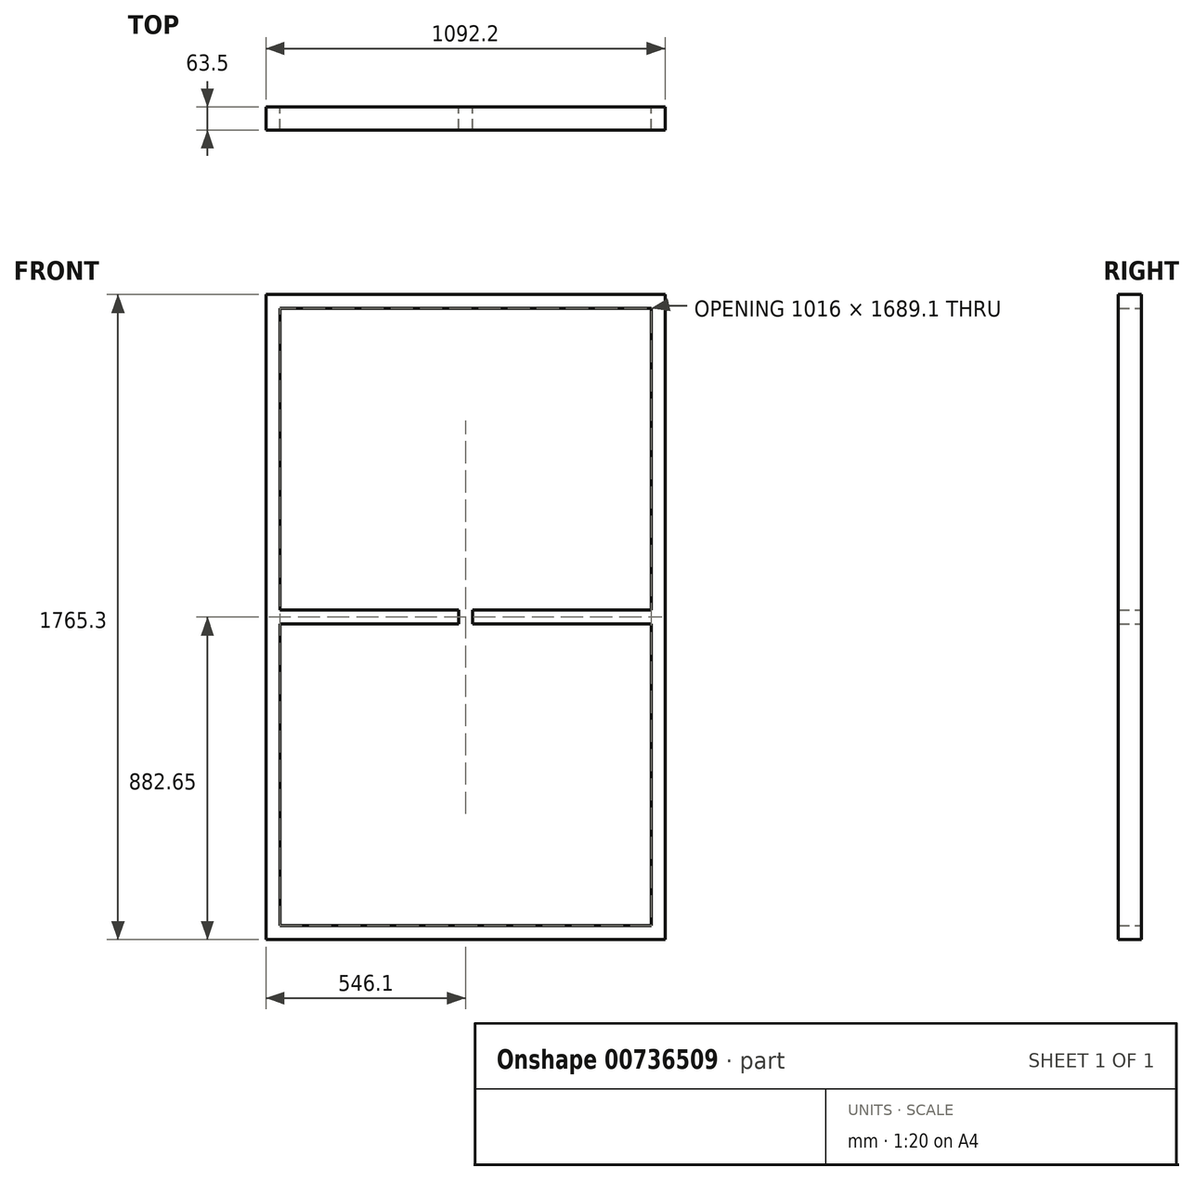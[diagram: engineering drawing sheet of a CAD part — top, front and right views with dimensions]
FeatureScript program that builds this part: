
annotation { "Feature Type Name" : "Feature", "Feature Type Description" : "" }
export const myFeature = defineFeature(function(context is Context, id is Id, definition is map)
    precondition{}
    {
        {
            var Q0;
            Q0=qCreatedBy(makeId("Front.planeOp"),FACE);
            var sketch = newSketch(context, id + "F0", { "sketchPlane" : qUnion([Q0])});
            skLineSegment(sketch, "E0.bottom", {"start": v(546.1, 882.65) * mm, "end": v(-546.1, 882.65) * mm});
            skLineSegment(sketch, "E0.top", {"start": v(546.1, -882.65) * mm, "end": v(-546.1, -882.65) * mm});
            skLineSegment(sketch, "E0.left", {"start": v(546.1, 882.65) * mm, "end": v(546.1, -882.65) * mm});
            skLineSegment(sketch, "E0.right", {"start": v(-546.1, 882.65) * mm, "end": v(-546.1, -882.65) * mm});
            skPoint(sketch, "E0.middle", {"position": v(0, 0) * mm});
            skLineSegment(sketch, "E1", {"start": v(-546.1, 844.55) * mm, "end": v(546.1, 844.55) * mm});
            skLineSegment(sketch, "E2", {"start": v(-546.1, -844.55) * mm, "end": v(546.1, -844.55) * mm});
            skLineSegment(sketch, "E3", {"start": v(-508, -844.55) * mm, "end": v(-508, 844.55) * mm});
            skLineSegment(sketch, "E4", {"start": v(508, -844.55) * mm, "end": v(508, 844.55) * mm});
            skLineSegment(sketch, "E5", {"start": v(-19.05, 844.55) * mm, "end": v(-19.05, -844.55) * mm});
            skLineSegment(sketch, "E6", {"start": v(19.05, 844.55) * mm, "end": v(19.05, -844.55) * mm});
            skLineSegment(sketch, "E7", {"start": v(0, 844.55) * mm, "end": v(0, -844.55) * mm, "construction": true});
            skLineSegment(sketch, "E8", {"start": v(-19.05, -844.55) * mm, "end": v(19.05, -844.55) * mm});
            skLineSegment(sketch, "E9", {"start": v(19.05, 19.05) * mm, "end": v(508, 19.05) * mm});
            skLineSegment(sketch, "E10", {"start": v(19.05, -19.05) * mm, "end": v(508, -19.05) * mm});
            skLineSegment(sketch, "E11", {"start": v(-19.05, 19.05) * mm, "end": v(-508, 19.05) * mm});
            skLineSegment(sketch, "E12", {"start": v(-508, -19.05) * mm, "end": v(-19.05, -19.05) * mm});
            skLineSegment(sketch, "E13", {"start": v(19.05, 19.05) * mm, "end": v(19.05, -19.05) * mm});
            skLineSegment(sketch, "E14", {"start": v(-19.05, 0) * mm, "end": v(19.05, 0) * mm, "construction": true});
            skLineSegment(sketch, "E15", {"start": v(-19.05, 19.05) * mm, "end": v(-19.05, -19.05) * mm});
            skSolve(sketch);
        }
        {
            var Q0;
            {var subQ4=sQuery(id+"F0.wireOp",EDGE,"E1");var subQ5=sQuery(id+"F0.wireOp",EDGE,"E0.right");var subQ6=makeQuery(id+"F0.imprint","INTERSECT",VERTEX,{"derivedFrom":[subQ5,subQ4]});Q0=makeQuery(id+"F0.imprint","IMPRINT",FACE,{"disambiguationData":[TD([[makeQuery(id+"F0.imprint","IMPRINT",EDGE,{"disambiguationData":[TD([[subQ6,-1.0]])],"derivedFrom":subQ5}),1.0]])]});}
            var Q1;
            {var subQ4=sQuery(id+"F0.wireOp",EDGE,"E0.left");var subQ6=sQuery(id+"F0.wireOp",EDGE,"E1");var subQ7=makeQuery(id+"F0.imprint","INTERSECT",VERTEX,{"derivedFrom":[subQ4,subQ6]});Q1=makeQuery(id+"F0.imprint","IMPRINT",FACE,{"disambiguationData":[TD([[makeQuery(id+"F0.imprint","IMPRINT",EDGE,{"disambiguationData":[TD([[subQ7,-1.0]])],"derivedFrom":subQ4}),-1.0]])]});}
            var Q2;
            {var subQ5=sQuery(id+"F0.wireOp",EDGE,"E0.bottom");Q2=makeQuery(id+"F0.imprint","IMPRINT",FACE,{"disambiguationData":[TD([[makeQuery(id+"F0.imprint","IMPRINT",EDGE,{"derivedFrom":subQ5}),1.0]])]});}
            var Q3;
            {var subQ0=sQuery(id+"F0.wireOp",EDGE,"E8");Q3=makeQuery(id+"F0.imprint","IMPRINT",FACE,{"disambiguationData":[TD([[makeQuery(id+"F0.imprint","IMPRINT",EDGE,{"derivedFrom":subQ0}),1.0]])]});}
            var Q4;
            {var subQ0=sQuery(id+"F0.wireOp",EDGE,"E9");Q4=makeQuery(id+"F0.imprint","IMPRINT",FACE,{"disambiguationData":[TD([[makeQuery(id+"F0.imprint","IMPRINT",EDGE,{"derivedFrom":subQ0}),-1.0]])]});}
            var Q5;
            {var subQ0=sQuery(id+"F0.wireOp",EDGE,"E11");Q5=makeQuery(id+"F0.imprint","IMPRINT",FACE,{"disambiguationData":[TD([[makeQuery(id+"F0.imprint","IMPRINT",EDGE,{"derivedFrom":subQ0}),1.0]])]});}
            var Q6;
            {var subQ4=sQuery(id+"F0.wireOp",EDGE,"E0.top");Q6=makeQuery(id+"F0.imprint","IMPRINT",FACE,{"disambiguationData":[TD([[makeQuery(id+"F0.imprint","IMPRINT",EDGE,{"derivedFrom":subQ4}),-1.0]])]});}
            extrude(context, id + "F1", {"entities" : qUnion([Q0, Q1, Q2, Q3, Q4, Q5, Q6]), "depth" : 63.5 * mm, "offsetDistance" : 25.4 * mm});
        }
    });
